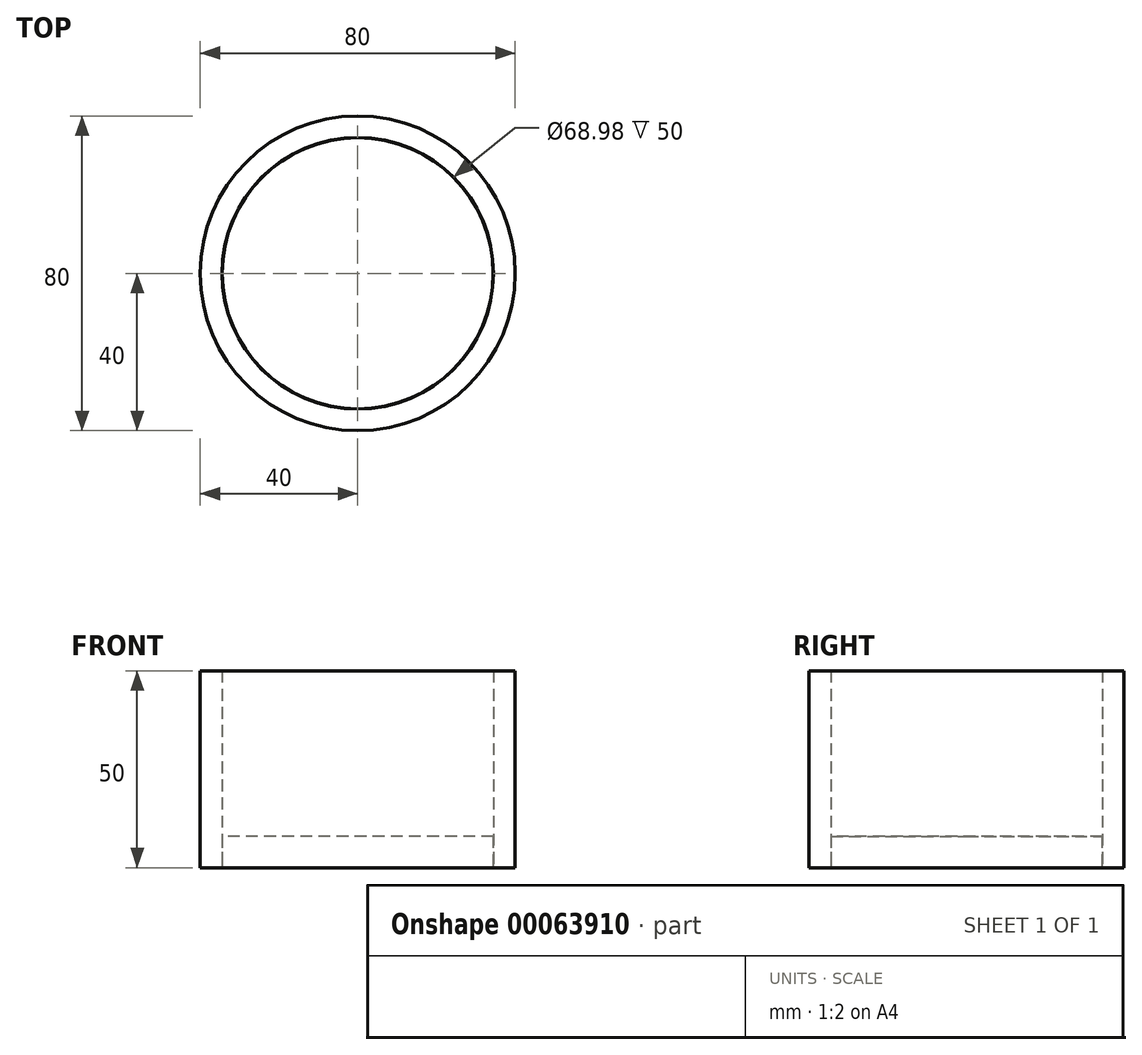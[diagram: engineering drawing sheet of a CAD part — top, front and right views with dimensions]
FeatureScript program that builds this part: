
annotation { "Feature Type Name" : "Feature", "Feature Type Description" : "" }
export const myFeature = defineFeature(function(context is Context, id is Id, definition is map)
    precondition{}
    {
        {
            var Q0;
            Q0=qCreatedBy(makeId("Top.planeOp"),FACE);
            var sketch = newSketch(context, id + "F0", { "sketchPlane" : qUnion([Q0])});
            skCircle(sketch, "E0", {"center": v(0, 0) * mm, "radius": 40 * mm});
            skCircle(sketch, "E1", {"center": v(0, 0) * mm, "radius": 34.49 * mm});
            skCircle(sketch, "E2", {"center": v(0, 0) * mm, "radius": 34.43 * mm});
            skSolve(sketch);
        }
        {
            var Q0;
            Q0=makeQuery(id+"F0.imprint","IMPRINT",FACE,{"disambiguationData":[TD([[makeQuery(id+"F0.imprint","IMPRINT",EDGE,{"derivedFrom":sQuery(id+"F0.wireOp",EDGE,"E0")}),1.0]])]});
            extrude(context, id + "F1", {"entities" : qUnion([Q0]), "depth" : 50 * mm});
        }
        {
            var Q0;
            Q0=makeQuery(id+"F0.imprint","IMPRINT",FACE,{"disambiguationData":[TD([[makeQuery(id+"F0.imprint","IMPRINT",EDGE,{"derivedFrom":sQuery(id+"F0.wireOp",EDGE,"E2")}),1.0]])]});
            extrude(context, id + "F2", {"entities" : qUnion([Q0]), "depth" : 8 * mm});
        }
    });
